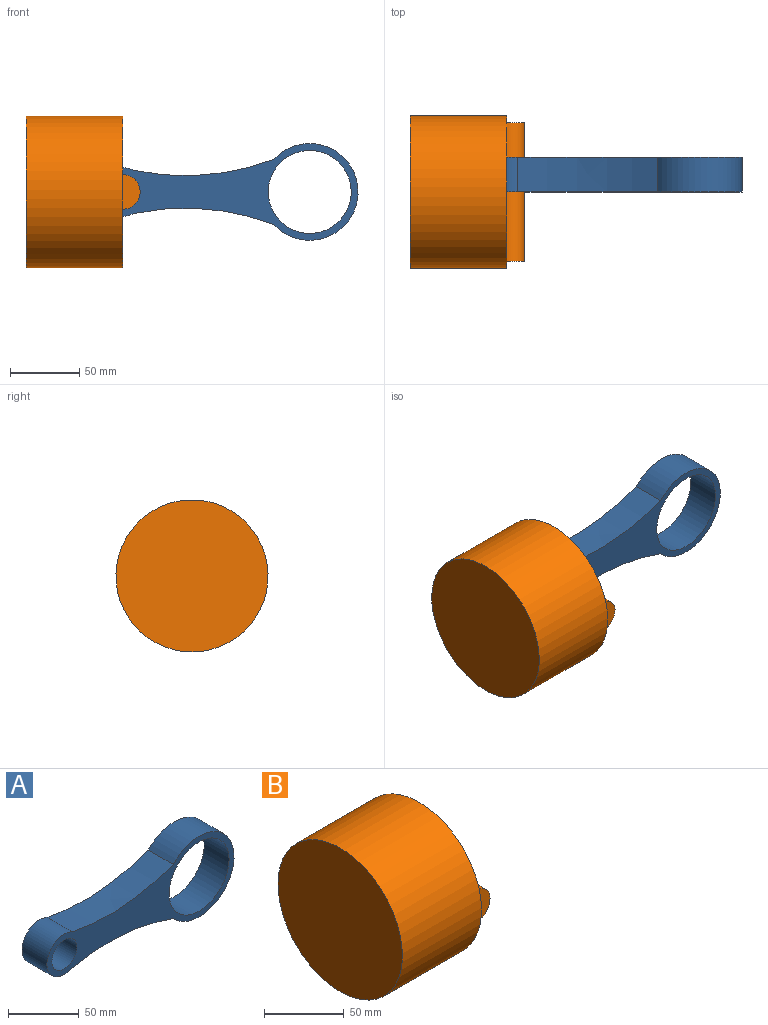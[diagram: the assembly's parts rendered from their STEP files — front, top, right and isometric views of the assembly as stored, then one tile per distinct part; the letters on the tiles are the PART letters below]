
ASSEMBLY  parts=2 mates=1
PART A: 8 faces, bbox 187.7x25x70 mm
  f0: cylinder r=17.5mm len=35mm, axis (0,1,0), area 1780.7mm2, adj f1,f4,f6,f7
  f1: extruded ~101.39x25mm, area 2577.5mm2, adj f0,f2,f6,f7
  f2: cylinder r=35mm len=70mm, axis (0,1,0), area 4209.5mm2, adj f1,f4,f6,f7
  f3: cylinder r=30mm len=60mm, axis (0,1,0), area 4712.4mm2, adj f6,f7
  f4: extruded ~101.39x25mm, area 2577.5mm2, adj f0,f2,f6,f7
  f5: cylinder r=12.5mm len=25mm, axis (0,1,0), area 1963.5mm2, adj f6,f7
  f6: plane 187.67x70mm, normal (0,-1,0), area 3954.6mm2, adj f0,f1,f2,f3,f4,f5
  f7: plane 187.67x70mm, normal (0,1,0), area 3954.6mm2, adj f0,f1,f2,f3,f4,f5
PART B: 8 faces, bbox 82.5x110x110 mm
  f0: cylinder r=55mm len=110mm, axis (-1,0,0), area 24190.3mm2, adj f1,f2
  f1: plane 110x110mm, normal (1,0,0), area 1623mm2, adj f0,f3,f5,f6,f7
  f2: plane 110x110mm, normal (-1,0,0), area 9503.3mm2, adj f0
  f3: cylinder r=50mm len=100mm, axis (1,0,0), area 18354.8mm2, adj f1,f4,f7
  f4: plane 100x100mm, normal (1,0,0), area 7854mm2, adj f3
  f5: plane 25x12.5mm, normal (0,1,0), area 245.4mm2, adj f1,f7
  f6: plane 25x12.5mm, normal (0,-1,0), area 245.4mm2, adj f1,f7
  f7: cylinder r=12.5mm len=100mm, axis (0,1,0), area 7791.9mm2, adj f1,f3,f5,f6
PLACE A t=(-91.09,66.58,26.74)mm
PLACE B t=(-20.04,58.2,-61.56)mm
MATE revolute A.f0 <-> B.f7  axis (0,-1,0) through (49.96,41.58,-51.19)mm
